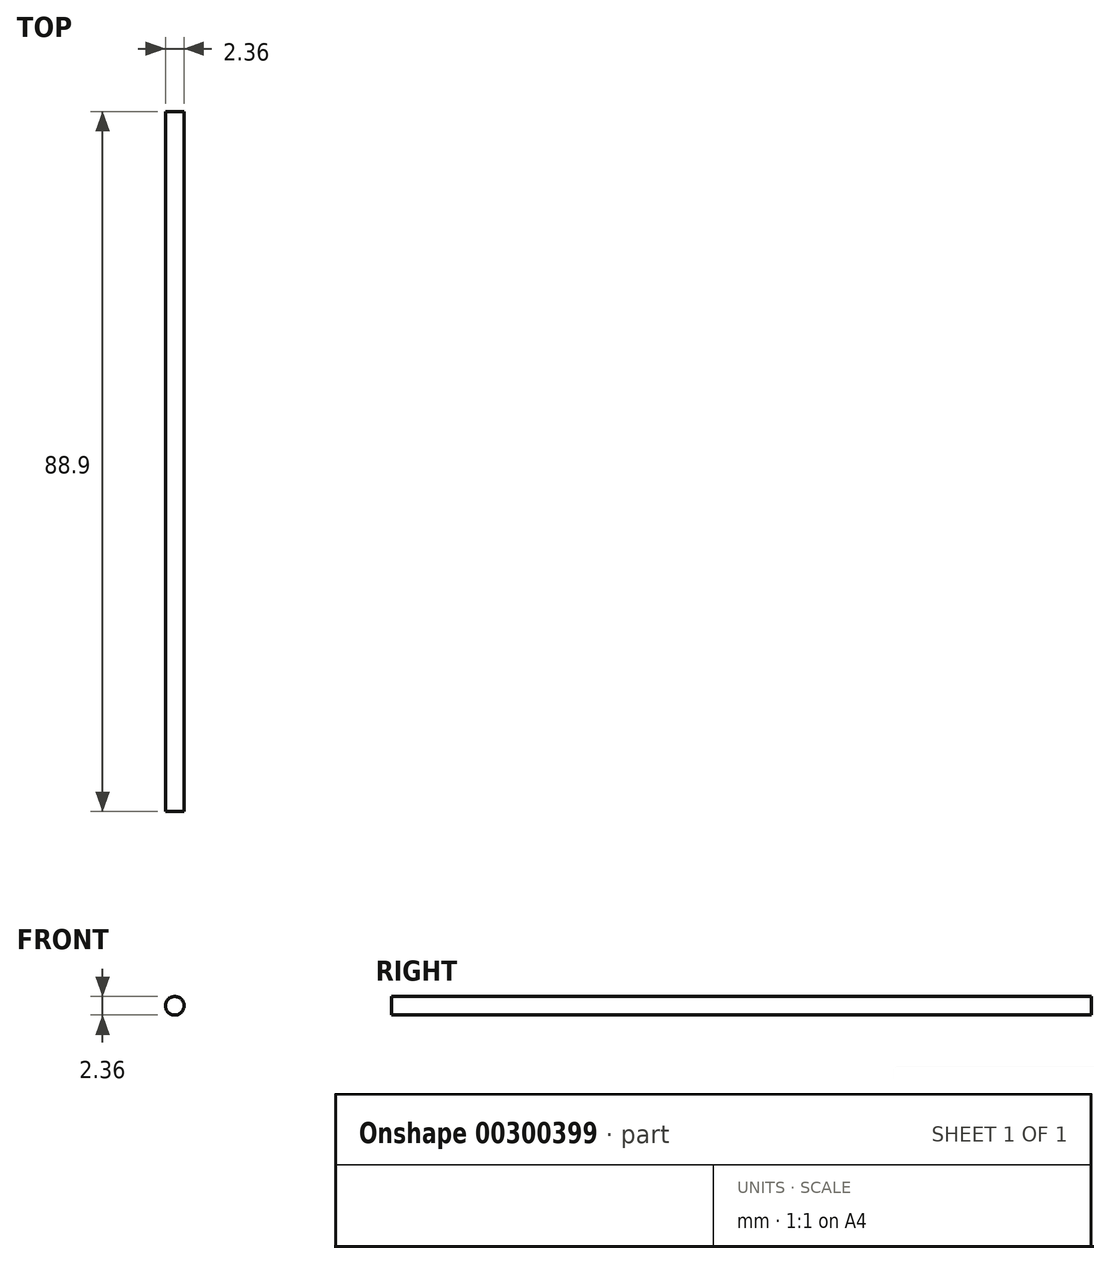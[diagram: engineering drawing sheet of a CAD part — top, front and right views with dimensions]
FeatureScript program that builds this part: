
annotation { "Feature Type Name" : "Feature", "Feature Type Description" : "" }
export const myFeature = defineFeature(function(context is Context, id is Id, definition is map)
    precondition{}
    {
        {
            var Q0;
            Q0=qCreatedBy(makeId("Front.planeOp"),FACE);
            var sketch = newSketch(context, id + "F0", { "sketchPlane" : qUnion([Q0])});
            skLineSegment(sketch, "E0.bottom", {"start": v(-1.18, 1.18) * mm, "end": v(1.18, 1.18) * mm, "construction": true});
            skLineSegment(sketch, "E0.top", {"start": v(-1.18, -1.18) * mm, "end": v(1.18, -1.18) * mm, "construction": true});
            skLineSegment(sketch, "E0.left", {"start": v(-1.18, 1.18) * mm, "end": v(-1.18, -1.18) * mm, "construction": true});
            skLineSegment(sketch, "E0.right", {"start": v(1.18, 1.18) * mm, "end": v(1.18, -1.18) * mm, "construction": true});
            skPoint(sketch, "E0.middle", {"position": v(0, 0) * mm});
            skCircle(sketch, "E1", {"center": v(0, 0) * mm, "radius": 1.18 * mm});
            skSolve(sketch);
        }
        {
            var Q0;
            Q0 = qSketchRegion(id + "F0", true);
            extrude(context, id + "F1", {"entities" : qUnion([Q0]), "endBound" : BoundingType.SYMMETRIC, "depth" : 88.9 * mm});
        }
    });
